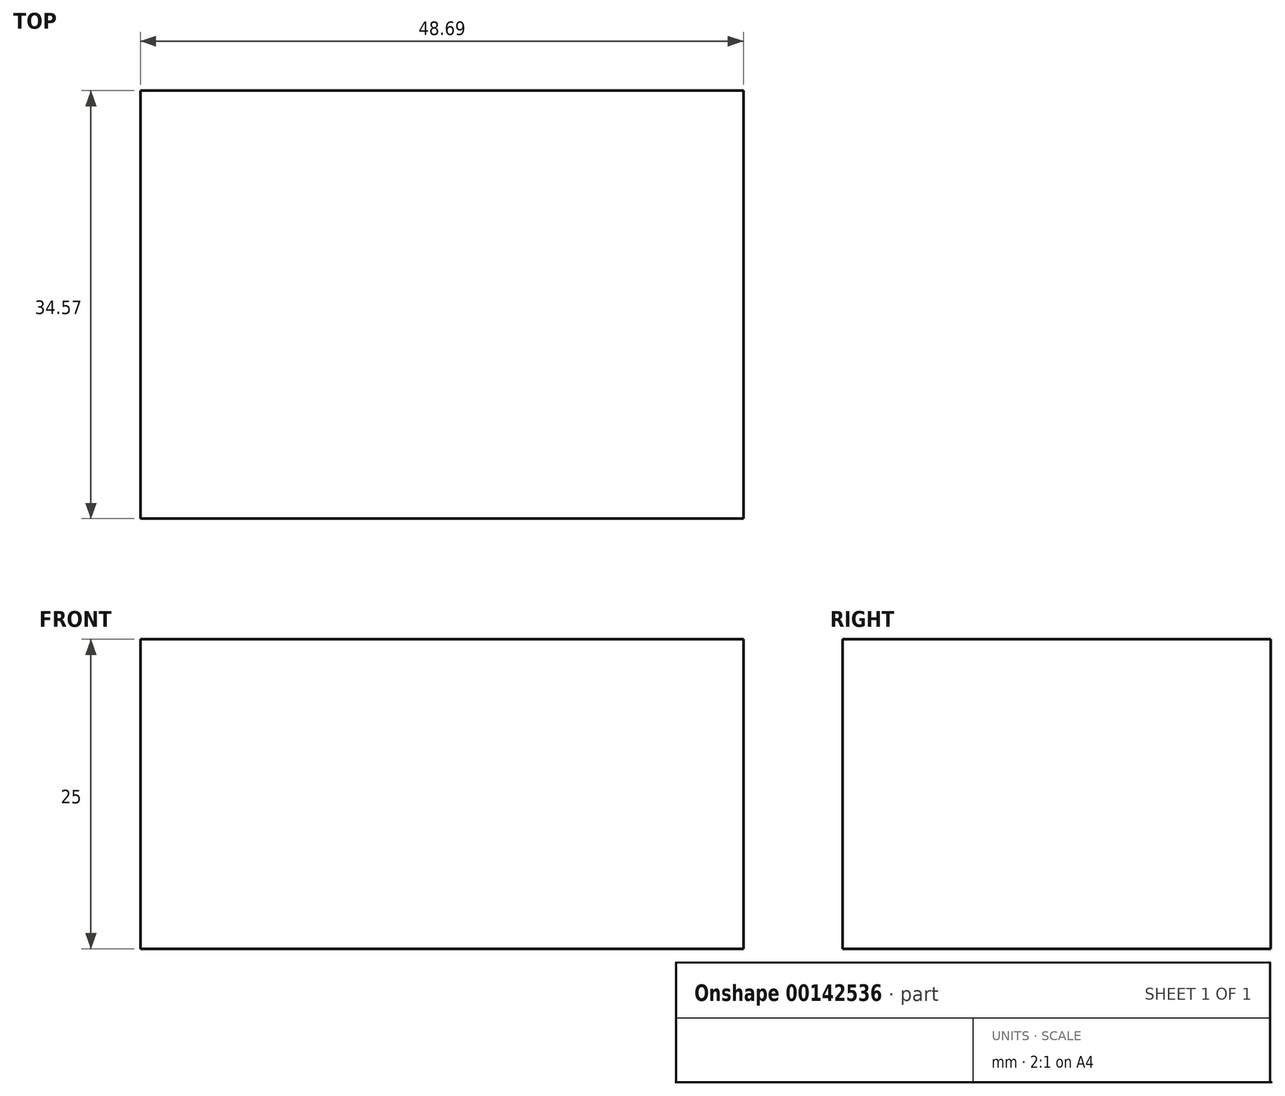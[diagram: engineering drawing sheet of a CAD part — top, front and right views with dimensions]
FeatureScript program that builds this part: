
annotation { "Feature Type Name" : "Feature", "Feature Type Description" : "" }
export const myFeature = defineFeature(function(context is Context, id is Id, definition is map)
    precondition{}
    {
        {
            var Q0;
            Q0=qCreatedBy(makeId("Top.planeOp"),FACE);
            var sketch = newSketch(context, id + "F0", { "sketchPlane" : qUnion([Q0])});
            skLineSegment(sketch, "E0.bottom", {"start": v(-23.22, 16.77) * mm, "end": v(25.47, 16.77) * mm});
            skLineSegment(sketch, "E0.top", {"start": v(-23.22, -17.8) * mm, "end": v(25.47, -17.8) * mm});
            skLineSegment(sketch, "E0.left", {"start": v(-23.22, 16.77) * mm, "end": v(-23.22, -17.8) * mm});
            skLineSegment(sketch, "E0.right", {"start": v(25.47, 16.77) * mm, "end": v(25.47, -17.8) * mm});
            skSolve(sketch);
        }
        {
            var Q0;
            Q0 = qSketchRegion(id + "F0", true);
            extrude(context, id + "F1", {"entities" : qUnion([Q0]), "depth" : 25 * mm});
        }
    });
